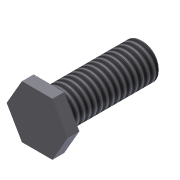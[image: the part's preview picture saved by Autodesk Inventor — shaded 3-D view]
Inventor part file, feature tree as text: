
AUTODESK INVENTOR PART (.ipt)
format: ipt  version: 2011 (Build 150239000, 239)  size: 97,280 bytes
history: native  units: in
note: dims shown in document units (in); Inventor stores cm internally (conversion verified against a paired STEP export)
features: extrude x2, sketch x2, thread x1, chamfer x1
ambient origin geometry x8: Origin, YZ Plane, XZ Plane, XY Plane, X Axis, Y Axis, Z Axis, Center Point
bodies: Solid1 (feature_tree)
feature tree (6):
  extrude  "Extrusion1"  Depth=1.0in TaperAngle=0.0deg
  extrude  "Extrusion2"  Depth=0.125in TaperAngle=0.0deg
  thread  "Thread1"  [1 undecoded]
  chamfer  "Chamfer1"  Distance=0.02in Angle=45.0deg
  sketch  "Sketch1"  dims[d0=0.375in d1=1.0in d2=0.0in]
  sketch  "Sketch2"  dims[d3=0.5625in d4=0.125in d5=0.0in d6=1.0in d7=0.0in d8=0.02in d9=0.125in d10=45.0deg]
note: 1 required parameter value undecoded (feature->parameter linkage not recoverable at this tier; creation-order binding heuristic only, values carry confidence <= 0.55)
